# Revit family: Spec  Equip_Grabrail_Argent_Advantage_Straight
name_source: partatom
category: Specialty Equipment
revit_build: Autodesk Revit 2016 (Build: 20150220_1215(x64)
units: mm (PartAtom-declared; Revit-internal decimal feet)

## family parameters
Always vertical = Yes
Cut with Voids When Loaded = No
OmniClass Number = 23.40.20.21.47
OmniClass Title = Bath Grab Bars
Part Type = Normal
Room Calculation Point = No
Round Connector Dimension = Use Diameter
Shared = No
Work Plane-Based = No

## types (6) — shared parameters
Body Material = z_Argent_Chrome
Description = Advantage Grab Rail
IfcExportAs = IfcRailing
IfcExportType = HANDRAIL
Manufacturer = Argent
Manufacturer_Overall Depth = 85 mm
Manufacturer_Overall Width = 80 mm
Manufacturer_URL__Product Specific = https://www.argentaust.com.au
ModifiedIssue_ANZRS = 20200402 $
URL = https://www.argentaust.com.au
Uniclass2015Code = Pr_40_20_76_84
Uniclass2015Title = Support rails
Uniclass2015Version = Products v1.17
zero-valued in all types: Cost

## per-type parameters (varying)
| type | Manufacturer_Overall Height | Manufacturer_Spec Code | Model | Type Comments |
| 450 Chrome (428845) | 530 mm | 428845 | 428845 | 450mm - Chrome Finish |
| 300 Chrome (428830) | 380 mm | 428830 | 428830 | 300mm - Chrome Finish |
| 600 Chrome (428860) | 680 mm | 428860 | 428860 | 600mm - Chrome Finish |
| 750 Chrome (428875) | 830 mm | 428875 | 428875 | 750mm - Chrome Finish |
| 900 Chrome (428890) | 980 mm | 428890 | 428890 | 900mm - Chrome Finish |
| 1000 Chrome (4281000) | 1080 mm | 4281000 | 4281000 | 1000mm - Chrome Finish |

## geometry (parser evidence)
native form markers: Sweep x2
no freeform markers — native parametric forms only
